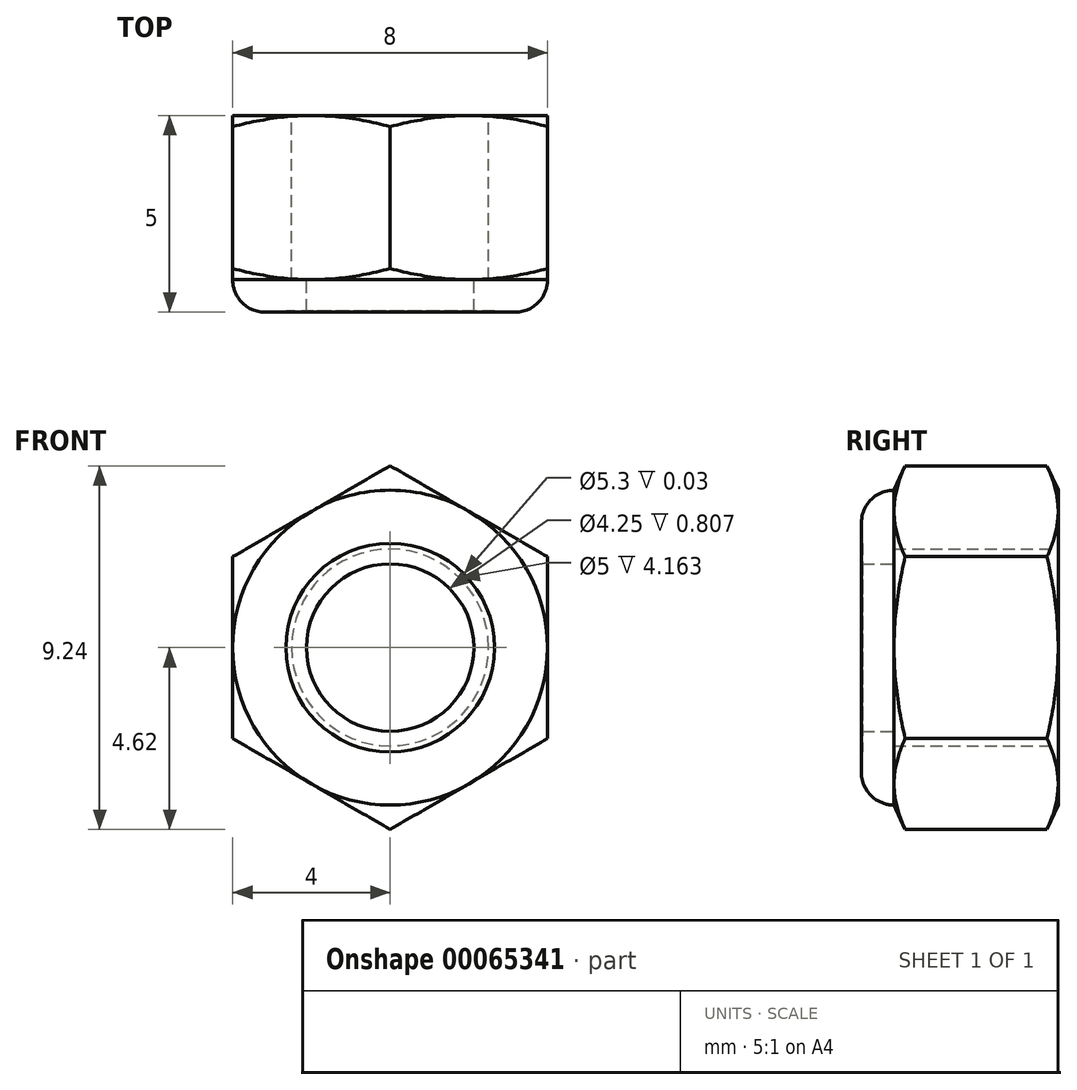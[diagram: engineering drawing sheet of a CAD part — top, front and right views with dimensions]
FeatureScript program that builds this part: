
annotation { "Feature Type Name" : "Feature", "Feature Type Description" : "" }
export const myFeature = defineFeature(function(context is Context, id is Id, definition is map)
    precondition{}
    {
        {
            var Q0;
            Q0=qCreatedBy(makeId("Right.planeOp"),FACE);
            var sketch = newSketch(context, id + "F0", { "sketchPlane" : qUnion([Q0])});
            skLineSegment(sketch, "E0", {"start": v(0, 0) * mm, "end": v(19.01, 0) * mm, "construction": true});
            skLineSegment(sketch, "E1", {"start": v(0, 6.95) * mm, "end": v(0.5, 6.95) * mm});
            skLineSegment(sketch, "E2", {"start": v(0.5, 6.95) * mm, "end": v(0.5, 7.99) * mm});
            skLineSegment(sketch, "E3", {"start": v(0.5, 7.99) * mm, "end": v(5.1, 7.99) * mm});
            skLineSegment(sketch, "E4", {"start": v(5.1, 7.99) * mm, "end": v(5.1, 9.8) * mm});
            skLineSegment(sketch, "E5", {"start": v(5.1, 9.8) * mm, "end": v(2.95, 11.96) * mm});
            skLineSegment(sketch, "E6", {"start": v(2.95, 11.96) * mm, "end": v(0, 11.96) * mm});
            skLineSegment(sketch, "E7", {"start": v(0, 0) * mm, "end": v(0, 11.96) * mm, "construction": true});
            skLineSegment(sketch, "E8.MirrorCS", {"start": v(0, 6.95) * mm, "end": v(-0.5, 6.95) * mm});
            skLineSegment(sketch, "E9.MirrorCS", {"start": v(-2.95, 11.96) * mm, "end": v(0, 11.96) * mm});
            skLineSegment(sketch, "E10.MirrorCS", {"start": v(-0.5, 6.95) * mm, "end": v(-0.5, 7.99) * mm});
            skLineSegment(sketch, "E11.MirrorCS", {"start": v(-5.1, 7.99) * mm, "end": v(-5.1, 9.8) * mm});
            skLineSegment(sketch, "E12.MirrorCS", {"start": v(-0.5, 7.99) * mm, "end": v(-5.1, 7.99) * mm});
            skLineSegment(sketch, "E13.MirrorCS", {"start": v(-5.1, 9.8) * mm, "end": v(-2.95, 11.96) * mm});
            skSolve(sketch);
        }
        {
            var Q0;
            Q0=qSketchRegion(id+"F0",true);
            var Q1;
            Q1=sQuery(id+"F0.wireOp",EDGE,"E0");
            revolve(context, id + "F1", {"entities" : qUnion([Q0]), "axis" : qUnion([Q1]), "revolveType" : RevolveType.FULL});
        }
        {
            var Q0;
            Q0=qCreatedBy(makeId("Front.planeOp"),FACE);
            var sketch = newSketch(context, id + "F2", { "sketchPlane" : qUnion([Q0])});
            skCircle(sketch, "E14", {"center": v(0, 0) * mm, "radius": 5 * mm});
            skCircle(sketch, "E15", {"center": v(0, 0) * mm, "radius": 2.5 * mm});
            skSolve(sketch);
        }
        {
            var Q0;
            Q0=qSketchRegion(id+"F2",true);
            extrude(context, id + "F3", {"entities" : qUnion([Q0]), "endBound" : BoundingType.SYMMETRIC, "depth" : 1 * mm});
        }
        {
            var Q0;
            Q0=qCreatedBy(makeId("Right.planeOp"),FACE);
            var sketch = newSketch(context, id + "F4", { "sketchPlane" : qUnion([Q0])});
            skLineSegment(sketch, "E16.0.0", {"start": v(-0.5, -5) * mm, "end": v(-0.5, 5) * mm, "construction": true});
            skLineSegment(sketch, "E17", {"start": v(-0.5, 2.5) * mm, "end": v(-5.5, 2.5) * mm});
            skLineSegment(sketch, "E18.MirrorCS", {"start": v(-0.5, 2.5) * mm, "end": v(-0.5, 4.3) * mm});
            skLineSegment(sketch, "E19.MirrorCS", {"start": v(-0.5, 4.3) * mm, "end": v(-0.8, 4.3) * mm});
            skLineSegment(sketch, "E20.MirrorCS", {"start": v(-0.8, 4.3) * mm, "end": v(-0.8, 6.8) * mm});
            skLineSegment(sketch, "E21", {"start": v(-0.8, 6.8) * mm, "end": v(-0.5, 6.8) * mm});
            skLineSegment(sketch, "E22", {"start": v(-0.5, 6.8) * mm, "end": v(-0.5, 8) * mm});
            skLineSegment(sketch, "E23", {"start": v(-0.5, 8) * mm, "end": v(-5.5, 8) * mm});
            skLineSegment(sketch, "E24", {"start": v(-3, 8) * mm, "end": v(-3, 2.5) * mm, "construction": true});
            skLineSegment(sketch, "E25.MirrorCS", {"start": v(-5.5, 6.8) * mm, "end": v(-5.5, 8) * mm});
            skLineSegment(sketch, "E26.MirrorCS", {"start": v(-5.5, 2.5) * mm, "end": v(-5.5, 4.3) * mm});
            skLineSegment(sketch, "E27.MirrorCS", {"start": v(-5.2, 4.3) * mm, "end": v(-5.2, 6.8) * mm});
            skLineSegment(sketch, "E28.MirrorCS", {"start": v(-5.2, 6.8) * mm, "end": v(-5.5, 6.8) * mm});
            skLineSegment(sketch, "E29.MirrorCS", {"start": v(-5.5, 4.3) * mm, "end": v(-5.2, 4.3) * mm});
            skLineSegment(sketch, "E30", {"start": v(0, 0) * mm, "end": v(-5.5, 0) * mm, "construction": true});
            skSolve(sketch);
        }
        {
            var Q0;
            Q0=qSketchRegion(id+"F4",true);
            var Q1;
            Q1=sQuery(id+"F4.wireOp",EDGE,"E30");
            revolve(context, id + "F5", {"entities" : qUnion([Q0]), "axis" : qUnion([Q1]), "revolveType" : RevolveType.FULL});
        }
        {
            var Q0;
            Q0=makeQuery(id+"F5.opRevolve","SWEPT_EDGE",EDGE,{"disambiguationData":[OSD([sQuery(id+"F4.wireOp",EDGE,"E23"),sQuery(id+"F4.wireOp",EDGE,"E25.MirrorCS")])]});
            var Q1;
            Q1=makeQuery(id+"F5.opRevolve","SWEPT_EDGE",EDGE,{"disambiguationData":[OSD([sQuery(id+"F4.wireOp",EDGE,"E22"),sQuery(id+"F4.wireOp",EDGE,"E23")])]});
            var Q2;
            Q2=makeQuery(id+"F5.opRevolve","SWEPT_EDGE",EDGE,{"disambiguationData":[OSD([sQuery(id+"F4.wireOp",EDGE,"E17"),sQuery(id+"F4.wireOp",EDGE,"E26.MirrorCS")])]});
            var Q3;
            Q3=makeQuery(id+"F5.opRevolve","SWEPT_EDGE",EDGE,{"disambiguationData":[OSD([sQuery(id+"F4.wireOp",EDGE,"E17"),sQuery(id+"F4.wireOp",EDGE,"E18.MirrorCS")])]});
            chamfer(context, id + "F6", {"entities" : qUnion([Q0, Q1, Q2, Q3]), "width" : 0.25 * mm, "tangentPropagation" : true});
        }
        {
            var Q0;
            Q0=qCreatedBy(makeId("Right.planeOp"),FACE);
            var sketch = newSketch(context, id + "F7", { "sketchPlane" : qUnion([Q0])});
            skLineSegment(sketch, "E31.0.0", {"start": v(-5.5, -4.3) * mm, "end": v(-5.5, 4.3) * mm, "construction": true});
            skLineSegment(sketch, "E32", {"start": v(-7.59, 8.6) * mm, "end": v(-7.59, -8) * mm, "construction": true});
            skLineSegment(sketch, "E33", {"start": v(-5.5, 4) * mm, "end": v(-5.79, 4.62) * mm});
            skLineSegment(sketch, "E34", {"start": v(-5.79, 4.62) * mm, "end": v(-7.59, 4.62) * mm});
            skLineSegment(sketch, "E35.MirrorCS", {"start": v(-9.39, 4.62) * mm, "end": v(-7.59, 4.62) * mm});
            skLineSegment(sketch, "E36.MirrorCS", {"start": v(-9.67, 4) * mm, "end": v(-9.39, 4.63) * mm});
            skLineSegment(sketch, "E37", {"start": v(-5.5, 0) * mm, "end": v(0, 0) * mm, "construction": true});
            skLineSegment(sketch, "E38", {"start": v(-5.5, 2.5) * mm, "end": v(-5.5, 4) * mm});
            skLineSegment(sketch, "E39", {"start": v(-5.5, 0) * mm, "end": v(-10.5, 0) * mm, "construction": true});
            skArc(sketch, "E40", {"start": v(-9.67, 4) * mm, "mid": v(-10.26, 3.76) * mm, "end": v(-10.5, 3.17) * mm});
            skLineSegment(sketch, "E41", {"start": v(-5.5, 2.5) * mm, "end": v(-9.66, 2.5) * mm});
            skLineSegment(sketch, "E42", {"start": v(-9.66, 2.5) * mm, "end": v(-9.66, 2.13) * mm});
            skLineSegment(sketch, "E43", {"start": v(-9.66, 2.13) * mm, "end": v(-10.47, 2.13) * mm});
            skLineSegment(sketch, "E44", {"start": v(-10.47, 2.13) * mm, "end": v(-10.47, 2.65) * mm});
            skLineSegment(sketch, "E45", {"start": v(-10.47, 2.65) * mm, "end": v(-10.5, 2.65) * mm});
            skLineSegment(sketch, "E46", {"start": v(-10.5, 2.65) * mm, "end": v(-10.5, 3.17) * mm});
            skLineSegment(sketch, "E47", {"start": v(-9.67, 4) * mm, "end": v(-5.5, 4) * mm, "construction": true});
            skSolve(sketch);
        }
        {
            var Q0;
            Q0=qSketchRegion(id+"F7",true);
            var Q1;
            Q1=sQuery(id+"F7.wireOp",EDGE,"E39");
            revolve(context, id + "F8", {"entities" : qUnion([Q0]), "axis" : qUnion([Q1]), "revolveType" : RevolveType.FULL});
        }
        {
            var Q0;
            Q0=makeQuery(id+"F8.opRevolve","SWEPT_FACE",FACE,{"disambiguationData":[OSD([sQuery(id+"F7.wireOp",EDGE,"E38")])]});
            var sketch = newSketch(context, id + "F9", { "sketchPlane" : qUnion([Q0])});
            skCircle(sketch, "E48.cCircle", {"center": v(0, 0) * mm, "radius": 4 * mm, "construction": true});
            skLineSegment(sketch, "E48.0", {"start": v(4, 2.3) * mm, "end": v(4, -2.3) * mm});
            skLineSegment(sketch, "E48.1", {"start": v(4, -2.3) * mm, "end": v(0, -4.62) * mm});
            skLineSegment(sketch, "E48.2", {"start": v(0, -4.62) * mm, "end": v(-4, -2.3) * mm});
            skLineSegment(sketch, "E48.3", {"start": v(-4, -2.3) * mm, "end": v(-4, 2.3) * mm});
            skLineSegment(sketch, "E48.4", {"start": v(-4, 2.3) * mm, "end": v(0, 4.62) * mm});
            skLineSegment(sketch, "E48.5", {"start": v(0, 4.62) * mm, "end": v(4, 2.3) * mm});
            skPoint(sketch, "E48.0.midPoint", {"position": v(4, 0) * mm});
            skSolve(sketch);
        }
        {
            var Q0;
            Q0=qSketchRegion(id+"F9",true);
            extrude(context, id + "F10", {"entities" : qUnion([Q0]), "operationType" : NewBodyOperationType.INTERSECT, "endBound" : BoundingType.THROUGH_ALL, "oppositeDirection" : true, "depth" : 25 * mm});
        }
    });
